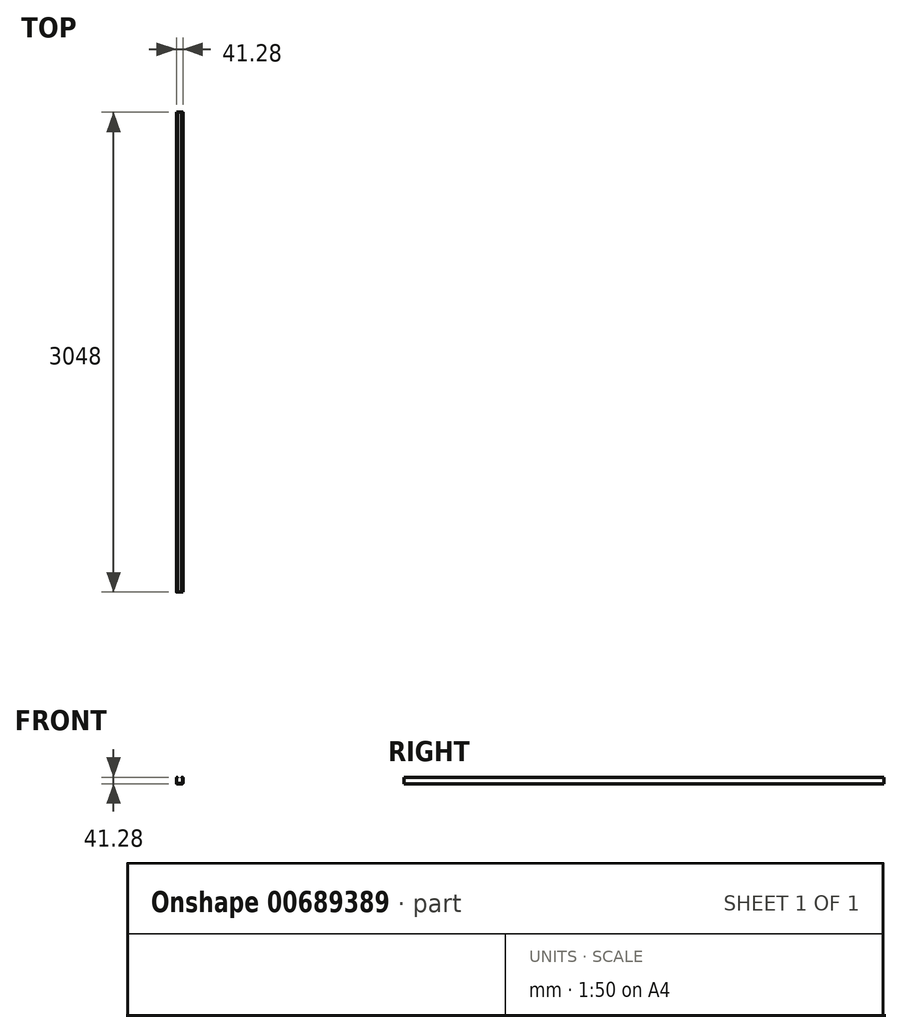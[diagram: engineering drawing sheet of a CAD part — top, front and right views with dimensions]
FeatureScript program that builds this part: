
annotation { "Feature Type Name" : "Feature", "Feature Type Description" : "" }
export const myFeature = defineFeature(function(context is Context, id is Id, definition is map)
    precondition{}
    {
        {
            var Q0;
            Q0=qCreatedBy(makeId("Front.planeOp"),FACE);
            var sketch = newSketch(context, id + "F0", { "sketchPlane" : qUnion([Q0])});
            skLineSegment(sketch, "E0.bottom", {"start": v(20.64, -20.64) * mm, "end": v(-20.64, -20.64) * mm});
            skLineSegment(sketch, "E0.left", {"start": v(20.64, -20.64) * mm, "end": v(20.64, 16.67) * mm});
            skPoint(sketch, "E0.middle", {"position": v(0, 0) * mm});
            skLineSegment(sketch, "E1.0", {"start": v(20.64, -19.05) * mm, "end": v(-20.64, -19.05) * mm});
            skLineSegment(sketch, "E2.0", {"start": v(19.05, -20.64) * mm, "end": v(19.05, 16.67) * mm});
            skLineSegment(sketch, "E3.0", {"start": v(-19.05, -20.64) * mm, "end": v(-19.05, 16.67) * mm});
            skArc(sketch, "E4", {"start": v(-12.7, 16.67) * mm, "mid": v(-16.67, 20.64) * mm, "end": v(-20.64, 16.67) * mm});
            skArc(sketch, "E5", {"start": v(-14.29, 16.67) * mm, "mid": v(-16.67, 19.05) * mm, "end": v(-19.05, 16.67) * mm});
            skArc(sketch, "E6.MirrorC", {"start": v(14.29, 16.67) * mm, "mid": v(16.67, 19.05) * mm, "end": v(19.05, 16.67) * mm});
            skArc(sketch, "E7.MirrorC", {"start": v(12.7, 16.67) * mm, "mid": v(16.67, 20.64) * mm, "end": v(20.64, 16.67) * mm});
            skLineSegment(sketch, "E8.trimOffspring", {"start": v(-14.29, 16.67) * mm, "end": v(-12.7, 16.67) * mm});
            skPoint(sketch, "E9.start.orphan", {"position": v(-19.05, 16.67) * mm});
            skPoint(sketch, "E10.orphan", {"position": v(-20.64, 20.64) * mm});
            skLineSegment(sketch, "E11.trimOffspring", {"start": v(12.7, 16.67) * mm, "end": v(14.29, 16.67) * mm});
            skLineSegment(sketch, "E12", {"start": v(-20.64, 16.67) * mm, "end": v(-20.64, -20.64) * mm});
            skPoint(sketch, "E0.top.start.orphan", {"position": v(20.64, 20.64) * mm});
            skSolve(sketch);
        }
        {
            var Q0;
            Q0 = qSketchRegion(id + "F0", true);
            extrude(context, id + "F1", {"entities" : qUnion([Q0]), "depth" : 3048 * mm, "offsetDistance" : 25.4 * mm, "symmetric" : true});
        }
        {
            var Q0;
            Q0=makeQuery(id+"F1.opExtrude","SWEPT_EDGE",EDGE,{"disambiguationData":[OSD([sQuery(id+"F0.wireOp",EDGE,"E1.0"),sQuery(id+"F0.wireOp",EDGE,"E3.0")])]});
            var Q1;
            Q1=makeQuery(id+"F1.opExtrude","SWEPT_EDGE",EDGE,{"disambiguationData":[OSD([sQuery(id+"F0.wireOp",EDGE,"E1.0"),sQuery(id+"F0.wireOp",EDGE,"E2.0")])]});
            var Q2;
            Q2=makeQuery(id+"F1.opExtrude","SWEPT_EDGE",EDGE,{"disambiguationData":[OSD([sQuery(id+"F0.wireOp",EDGE,"E0.bottom"),sQuery(id+"F0.wireOp",EDGE,"E0.left")])]});
            var Q3;
            Q3=makeQuery(id+"F1.opExtrude","SWEPT_EDGE",EDGE,{"disambiguationData":[OSD([sQuery(id+"F0.wireOp",EDGE,"E0.bottom"),sQuery(id+"F0.wireOp",EDGE,"E12")])]});
            fillet(context, id + "F2", {"entities" : qUnion([Q0, Q1, Q2, Q3]), "radius" : 1.59 * mm, "tangentPropagation" : true, "allowEdgeOverflow" : false});
        }
    });
